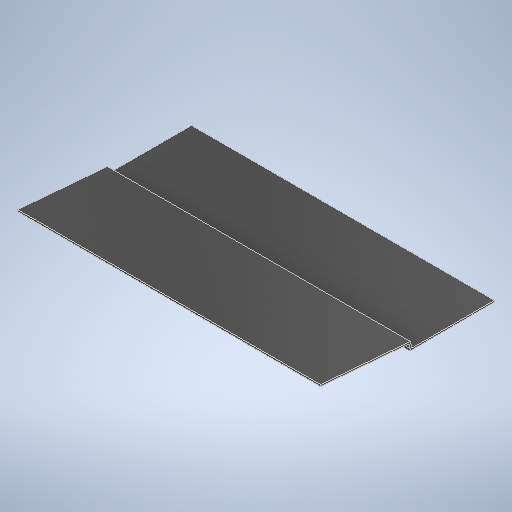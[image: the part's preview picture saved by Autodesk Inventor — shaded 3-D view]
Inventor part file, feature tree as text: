
AUTODESK INVENTOR PART (.ipt)
format: ipt  version: 2025.1 (Build 291241020, 241B)  size: 290,816 bytes
history: native  units: in
note: dims shown in document units (in); Inventor stores cm internally (conversion verified against a paired STEP export)
features: extrude x1, sketch x1
ambient origin geometry x8: Origin, YZ Plane, XZ Plane, XY Plane, X Axis, Y Axis, Z Axis, Center Point
bodies: Body1 (feature_tree)
feature tree (2):
  extrude  "Extrusion3"  Depth=0.125in
  sketch  "Sketch1"  dims[d0=23.408in d1=0.125in d2=0.265in d7=0.125in d8=0.237in d9=1.1431in d10=0.125in d11=0.7449in d12=0.125in d13=12.09in d18=0.125in d20=12.0907in d21=0.3425in d22=0.125in d23=0.125in d24=0.1549in d25=0.661in d28=0.125in d29=0.1254in d30=0.125in d32=0.125in d33=0.125in d34=5.625in d35=6.6451in d36=0.4476in d37=0.0449in d38=6.112in d39=22.375in d40=0.0in]
